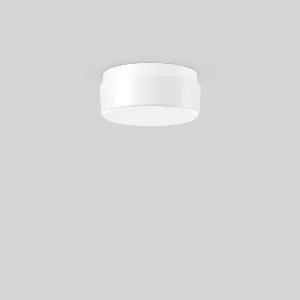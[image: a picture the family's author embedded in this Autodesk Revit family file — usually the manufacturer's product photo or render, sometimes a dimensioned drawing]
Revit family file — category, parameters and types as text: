
# Revit family: kreis_211416_002_1_b86c
name_source: partatom
category: Lighting Fixtures
units: mm (PartAtom-declared; Revit-internal decimal feet)

## family parameters
Cut with Voids When Loaded = No
Host = Face
Light Source = No
Part Type = Normal
Room Calculation Point = No
Round Connector Dimension = Use Diameter
Shared = No

## types (1)
- KREIS (1 x LED Modul 840, 1200 lm, 4000)
    Apparent Load = 11 VA
    CIE Flux Codes = 38 68 88 79 100
    Color Rendering = 80
    Color Temperature = 4000
    Default Elevation = 1800 mm
    Description = Series: KREIS
Round surface-mounted luminaire in classic design. Base: plastic. Opal glass: mouth-blown, satin finish. Diffuser fastening: spring system. Suitable for Ceiling mounting, Wall (surface). IP 43 ceiling mounting, IP 44 wall mounting. 
Colour: white
Diameter: 280 mm
Height: 120 mm
Lamp: LED exchangeable
Socket: without socket
Colour temperature: 4000K
Colour rendering index (CRI): 80
System power: 11 W
Rated luminous flux: 1200 lm
Luminous efficiency: 109 lm/W
Control gear: AC Strom, dim.Ph.an-/abschnitt
Protection class: I
Type of protection: IP 43
    Height = 120 mm
    Lamp = 1 x LED Modul 840
    Lamp Light Flux = 1200 lm
    Lamp count = 1
    Length = 280 mm
    Lifetime = 50000 h
    Luminous efficacy = 109 lm/W
    Manufacturer = RZB
    ModVariant = No
    Model = 211416.002.1
    Mounting Place = Ceiling, Wall
    Mounting Type = Surface mounted
    Number of Poles = 1
    OnlyDefault = Yes
    Power Factor = 1
    Product Name = KREIS
    Product group = Surface mounted ceiling and wall luminaires
    ProductGroupID = 305
    Protection Class = Protection class I
    Protection Degree = IP 43
    RLX_Detail_Level = 1
    RLX_Emergency_Light_Flux = 0 lm
    RLX_Emergency_Type = 0
    RLX_Emergency_Type_DB = No
    RlxData = <blob elided: 11661 chars, md5=c57ee421>
    Socket = socket
    Standby Power = 0 W
    System Light Flux = 1200 lm
    System Power = 11 W
    Type Comments = Product without accessories
    Type Image = 21171.002.jpg
    URL = http://relux.com
    VarID = ---
    Voltage = 230 V
    Voltage Range = 220-240 V
    Weight = 0.00 kg
    Width = 0 mm  [stored 0 ft]

note: [stored X ft] marks values corroborated as IEEE doubles in the binary element streams (Revit-internal decimal feet)

## geometry (parser evidence)
native form markers: Sweep x10
no freeform markers — native parametric forms only
